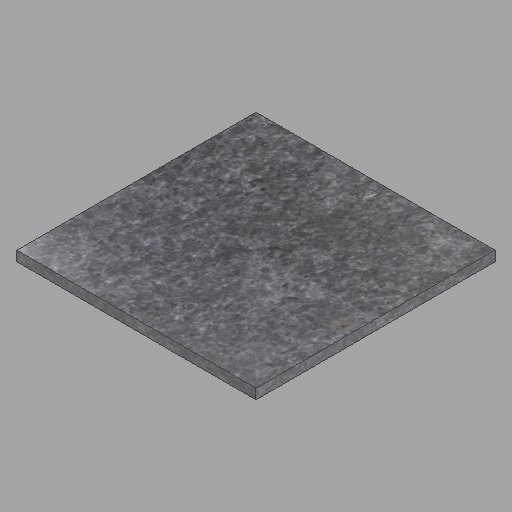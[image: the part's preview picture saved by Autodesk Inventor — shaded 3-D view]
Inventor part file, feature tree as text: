
AUTODESK INVENTOR PART (.ipt)
format: ipt  version: 2023 (Build 270158000, 158)  size: 239,104 bytes
history: native  units: in
note: dims shown in document units (in); Inventor stores cm internally (conversion verified against a paired STEP export)
features: other x1, extrude x1, sketch x1
ambient origin geometry x8: Origin, YZ Plane, XZ Plane, XY Plane, X Axis, Y Axis, Z Axis, Center Point
bodies: Solid1 (feature_tree)
feature tree (3):
  other  "24x24x2-75"
  extrude  "Extrusion1"  Depth=24.0in
  sketch  "Sketch1"  dims[d0=24.0in d1=24.0in d2=1.0in d3=0.0in]
